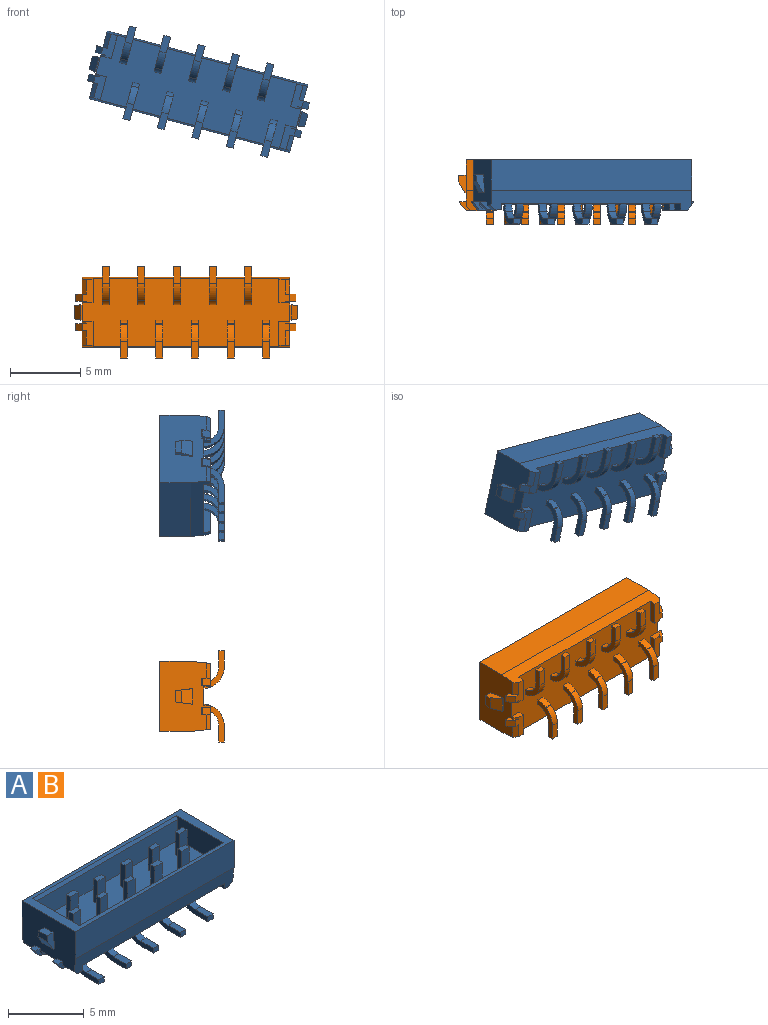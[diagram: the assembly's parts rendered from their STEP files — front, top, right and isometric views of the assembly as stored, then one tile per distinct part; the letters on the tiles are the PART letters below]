
ASSEMBLY  parts=2 mates=1
PART A: 227 faces, bbox 15.9x6.5x4.6 mm
  f0: plane 5x3.3mm, normal (-1,0,0), area 14.7mm2, adj f1,f3,f5,f6,f7,f8,f11,f14
  f1: plane 1.25x0.55mm, normal (0,0.99,0.12), area 0.5mm2, adj f0,f2,f4,f5,f6
  f2: plane 1.11x0.78mm, normal (-0.87,0,-0.5), area 0.9mm2, adj f1,f3,f4,f6
  f3: plane 1.25x0.55mm, normal (0,-0.99,0.12), area 0.5mm2, adj f0,f2,f4,f5,f6
  f4: plane 0.92x0.47mm, normal (-1,0,0), area 0.4mm2, adj f1,f2,f3,f5
  f5: plane 0.8x0.55mm, normal (0,0,1), area 0.4mm2, adj f0,f1,f3,f4
  f6: plane 1.11x0.1mm, normal (0,0,-1), area 0.1mm2, adj f0,f1,f2,f3
  f7: plane 0.5x0.45mm, normal (0,0,1), area 0.2mm2, adj f0,f11,f45,f46
  f8: plane 0.5x0.45mm, normal (0,0,1), area 0.2mm2, adj f0,f14,f112,f113
  f9: plane 0.5x0.45mm, normal (0,0,1), area 0.2mm2, adj f28,f224,f225,f226
  f10: plane 0.5x0.45mm, normal (0,0,1), area 0.2mm2, adj f21,f22,f23,f28
  f11: plane 0.75x0.6mm, normal (0,-1,0), area 0.2mm2, adj f0,f7,f13,f18,f41,f46
  f12: plane 0.54x0.5mm, normal (-0.77,0,-0.64), area 0.4mm2, adj f14,f17,f112,f113
  f13: plane 0.54x0.5mm, normal (-0.77,0,-0.64), area 0.4mm2, adj f11,f18,f45,f46
  f14: plane 0.75x0.6mm, normal (0,1,0), area 0.2mm2, adj f0,f8,f12,f17,f44,f113
  f15: plane 1.68x0.78mm, normal (0,0,-1), area 0.9mm2, adj f19,f21,f23,f24,f25,f35,f48,f51
  f16: plane 1.68x0.78mm, normal (0,0,-1), area 0.9mm2, adj f20,f26,f27,f40,f47,f49,f224,f226
  f17: plane 1.68x0.78mm, normal (0,0,-1), area 0.9mm2, adj f12,f14,f35,f36,f43,f44,f50,f112
  f18: plane 1.68x0.78mm, normal (0,0,-1), area 0.9mm2, adj f11,f13,f37,f39,f41,f42,f45,f47
  f19: plane 0.54x0.5mm, normal (0.77,0,-0.64), area 0.4mm2, adj f15,f21,f22,f23
  f20: plane 0.54x0.5mm, normal (0.77,0,-0.64), area 0.4mm2, adj f16,f224,f225,f226
  f21: plane 0.75x0.6mm, normal (0,1,0), area 0.2mm2, adj f10,f15,f19,f22,f24,f28
  f22: plane 0.5x0.06mm, normal (1,0,0), area 0mm2, adj f10,f19,f21,f23
  f23: plane 0.75x0.6mm, normal (0,-1,0), area 0.2mm2, adj f10,f15,f19,f22,f25,f28
  f24: plane 0.3x0.3mm, normal (0.71,0,-0.71), area 0.1mm2, adj f15,f21,f28,f51
  f25: plane 1.08x0.3mm, normal (0.71,0,-0.71), area 0.5mm2, adj f15,f23,f28,f35
  f26: plane 1.08x0.3mm, normal (0.71,0,-0.71), area 0.5mm2, adj f16,f28,f47,f224
  f27: plane 0.3x0.3mm, normal (0.71,0,-0.71), area 0.1mm2, adj f16,f28,f40,f226
  f28: plane 5x3.3mm, normal (1,0,0), area 14.7mm2, adj f9,f10,f21,f23,f24,f25,f26,f27
  f29: plane 1.25x0.55mm, normal (0,0.99,0.12), area 0.5mm2, adj f28,f30,f31,f33,f34
  f30: plane 1.11x0.78mm, normal (0.87,0,-0.5), area 0.9mm2, adj f29,f31,f32,f34
  f31: plane 1.11x0.1mm, normal (0,0,-1), area 0.1mm2, adj f28,f29,f30,f32
  f32: plane 1.25x0.55mm, normal (0,-0.99,0.12), area 0.5mm2, adj f28,f30,f31,f33,f34
  f33: plane 0.8x0.55mm, normal (0,0,1), area 0.4mm2, adj f28,f29,f32,f34
  f34: plane 0.92x0.47mm, normal (1,0,0), area 0.4mm2, adj f29,f30,f32,f33
  f35: plane 14.78x1.4mm, normal (0,-0.99,-0.1), area 14.7mm2, adj f0,f15,f17,f25,f28,f36,f38,f43
  f36: plane 1.73x0.45mm, normal (1,0,0), area 0.8mm2, adj f17,f35,f38,f50
  f37: plane 1.73x0.45mm, normal (1,0,0), area 0.8mm2, adj f18,f38,f39,f47
  f38: plane 14.78x4.8mm, normal (0,0,-1), area 63.6mm2, adj f0,f28,f35,f36,f37,f39,f40,f47
  f39: plane 0.78x0.45mm, normal (0,-1,0), area 0.3mm2, adj f0,f18,f37,f38,f41
  f40: plane 0.78x0.45mm, normal (0,-1,0), area 0.3mm2, adj f16,f27,f28,f38,f49
  f41: plane 0.3x0.3mm, normal (-0.71,0,-0.71), area 0.1mm2, adj f0,f11,f18,f39
  f42: plane 1.08x0.3mm, normal (-0.71,0,-0.71), area 0.5mm2, adj f0,f18,f45,f47
  f43: plane 1.08x0.3mm, normal (-0.71,0,-0.71), area 0.5mm2, adj f0,f17,f35,f112
  f44: plane 0.3x0.3mm, normal (-0.71,0,-0.71), area 0.1mm2, adj f0,f14,f17,f50
  f45: plane 0.75x0.6mm, normal (0,1,0), area 0.2mm2, adj f0,f7,f13,f18,f42,f46
  f46: plane 0.5x0.06mm, normal (-1,0,0), area 0mm2, adj f7,f11,f13,f45
  f47: plane 14.78x1.4mm, normal (0,0.99,-0.1), area 14.7mm2, adj f0,f16,f18,f26,f28,f37,f38,f42
  f48: plane 1.73x0.45mm, normal (-1,0,0), area 0.8mm2, adj f15,f35,f38,f51
  f49: plane 1.73x0.45mm, normal (-1,0,0), area 0.8mm2, adj f16,f38,f40,f47
  f50: plane 0.78x0.45mm, normal (0,1,0), area 0.3mm2, adj f0,f17,f36,f38,f44
  f51: plane 0.78x0.45mm, normal (0,1,0), area 0.3mm2, adj f15,f24,f28,f38,f48
  f52: plane 14.78x2.2mm, normal (0,1,0), area 32.5mm2, adj f0,f28,f47,f53
  f53: plane 14.78x5mm, normal (0,0,1), area 15mm2, adj f0,f28,f52,f54,f55,f58,f59,f60
  f54: plane 14.78x2.2mm, normal (0,-1,0), area 32.5mm2, adj f0,f28,f35,f53
  f55: plane 4.4x1.85mm, normal (-1,0,0), area 7.6mm2, adj f53,f56,f57,f58,f60,f61
  f56: plane 13.38x4mm, normal (0,0,1), area 50.8mm2, adj f55,f57,f59,f61,f62,f63,f64,f66
  f57: plane 13.38x1.61mm, normal (0,1,0.04), area 21.5mm2, adj f55,f56,f58,f59
  f58: plane 13.38x0.24mm, normal (0,0.87,0.5), area 3.7mm2, adj f53,f55,f57,f59
  f59: plane 4.4x1.85mm, normal (1,0,0), area 7.6mm2, adj f53,f56,f57,f58,f60,f61
  f60: plane 13.38x0.24mm, normal (0,-0.87,0.5), area 3.7mm2, adj f53,f55,f59,f61
  f61: plane 13.38x1.61mm, normal (0,-1,0.04), area 21.5mm2, adj f55,f56,f59,f60
  f62: plane 1.85x0.7mm, normal (0,1,0), area 1.3mm2, adj f56,f63,f65,f66
  f63: plane 1.85x0.39mm, normal (1,0,0), area 0.7mm2, adj f56,f62,f64,f65
  f64: plane 1.85x0.7mm, normal (0,-1,0), area 1.3mm2, adj f56,f63,f65,f66
  f65: plane 0.7x0.39mm, normal (0,0,1), area 0.3mm2, adj f62,f63,f64,f66
  f66: plane 1.85x0.39mm, normal (-1,0,0), area 0.7mm2, adj f56,f62,f64,f65
  f67: plane 1.85x0.7mm, normal (0,-1,0), area 1.3mm2, adj f56,f68,f70,f71
  f68: plane 1.85x0.39mm, normal (-1,0,0), area 0.7mm2, adj f56,f67,f69,f70
  f69: plane 1.85x0.7mm, normal (0,1,0), area 1.3mm2, adj f56,f68,f70,f71
  f70: plane 0.7x0.39mm, normal (0,0,1), area 0.3mm2, adj f67,f68,f69,f71
  f71: plane 1.85x0.39mm, normal (1,0,0), area 0.7mm2, adj f56,f67,f69,f70
  f72: plane 1.85x0.7mm, normal (0,1,0), area 1.3mm2, adj f56,f73,f75,f76
  f73: plane 1.85x0.39mm, normal (1,0,0), area 0.7mm2, adj f56,f72,f74,f75
  f74: plane 1.85x0.7mm, normal (0,-1,0), area 1.3mm2, adj f56,f73,f75,f76
  f75: plane 0.7x0.39mm, normal (0,0,1), area 0.3mm2, adj f72,f73,f74,f76
  f76: plane 1.85x0.39mm, normal (-1,0,0), area 0.7mm2, adj f56,f72,f74,f75
  f77: plane 1.85x0.7mm, normal (0,-1,0), area 1.3mm2, adj f56,f78,f80,f81
  f78: plane 1.85x0.39mm, normal (-1,0,0), area 0.7mm2, adj f56,f77,f79,f80
  f79: plane 1.85x0.7mm, normal (0,1,0), area 1.3mm2, adj f56,f78,f80,f81
  f80: plane 0.7x0.39mm, normal (0,0,1), area 0.3mm2, adj f77,f78,f79,f81
  f81: plane 1.85x0.39mm, normal (1,0,0), area 0.7mm2, adj f56,f77,f79,f80
  f82: plane 1.85x0.7mm, normal (0,1,0), area 1.3mm2, adj f56,f83,f85,f86
  f83: plane 1.85x0.39mm, normal (1,0,0), area 0.7mm2, adj f56,f82,f84,f85
  f84: plane 1.85x0.7mm, normal (0,-1,0), area 1.3mm2, adj f56,f83,f85,f86
  f85: plane 0.7x0.39mm, normal (0,0,1), area 0.3mm2, adj f82,f83,f84,f86
  f86: plane 1.85x0.39mm, normal (-1,0,0), area 0.7mm2, adj f56,f82,f84,f85
  f87: plane 1.85x0.7mm, normal (0,-1,0), area 1.3mm2, adj f56,f88,f90,f91
  f88: plane 1.85x0.39mm, normal (-1,0,0), area 0.7mm2, adj f56,f87,f89,f90
  f89: plane 1.85x0.7mm, normal (0,1,0), area 1.3mm2, adj f56,f88,f90,f91
  f90: plane 0.7x0.39mm, normal (0,0,1), area 0.3mm2, adj f87,f88,f89,f91
  f91: plane 1.85x0.39mm, normal (1,0,0), area 0.7mm2, adj f56,f87,f89,f90
  f92: plane 1.85x0.7mm, normal (0,1,0), area 1.3mm2, adj f56,f93,f95,f96
  f93: plane 1.85x0.39mm, normal (1,0,0), area 0.7mm2, adj f56,f92,f94,f95
  f94: plane 1.85x0.7mm, normal (0,-1,0), area 1.3mm2, adj f56,f93,f95,f96
  f95: plane 0.7x0.39mm, normal (0,0,1), area 0.3mm2, adj f92,f93,f94,f96
  f96: plane 1.85x0.39mm, normal (-1,0,0), area 0.7mm2, adj f56,f92,f94,f95
  f97: plane 1.85x0.7mm, normal (0,-1,0), area 1.3mm2, adj f56,f98,f100,f101
  f98: plane 1.85x0.39mm, normal (-1,0,0), area 0.7mm2, adj f56,f97,f99,f100
  f99: plane 1.85x0.7mm, normal (0,1,0), area 1.3mm2, adj f56,f98,f100,f101
  f100: plane 0.7x0.39mm, normal (0,0,1), area 0.3mm2, adj f97,f98,f99,f101
  f101: plane 1.85x0.39mm, normal (1,0,0), area 0.7mm2, adj f56,f97,f99,f100
  f102: plane 1.85x0.7mm, normal (0,1,0), area 1.3mm2, adj f56,f103,f105,f106
  f103: plane 1.85x0.39mm, normal (1,0,0), area 0.7mm2, adj f56,f102,f104,f105
  f104: plane 1.85x0.7mm, normal (0,-1,0), area 1.3mm2, adj f56,f103,f105,f106
  f105: plane 0.7x0.39mm, normal (0,0,1), area 0.3mm2, adj f102,f103,f104,f106
  f106: plane 1.85x0.39mm, normal (-1,0,0), area 0.7mm2, adj f56,f102,f104,f105
  f107: plane 1.85x0.7mm, normal (0,-1,0), area 1.3mm2, adj f56,f108,f110,f111
  f108: plane 1.85x0.39mm, normal (-1,0,0), area 0.7mm2, adj f56,f107,f109,f110
  f109: plane 1.85x0.7mm, normal (0,1,0), area 1.3mm2, adj f56,f108,f110,f111
  f110: plane 0.7x0.39mm, normal (0,0,1), area 0.3mm2, adj f107,f108,f109,f111
  f111: plane 1.85x0.39mm, normal (1,0,0), area 0.7mm2, adj f56,f107,f109,f110
  f112: plane 0.75x0.6mm, normal (0,-1,0), area 0.2mm2, adj f0,f8,f12,f17,f43,f113
  f113: plane 0.5x0.06mm, normal (-1,0,0), area 0mm2, adj f8,f12,f14,f112
  f114: plane 2.69x1.45mm, normal (-1,0,0), area 1.2mm2, adj f38,f115,f117,f118,f119,f120,f121,f122
  f115: cylinder r=1.5mm len=0.77mm, axis (1,0,0), area 0.4mm2, adj f38,f114,f116,f124
  f116: plane 2.69x1.45mm, normal (1,0,0), area 1.2mm2, adj f38,f115,f117,f118,f119,f120,f121,f122
  f117: cylinder r=1.11mm len=0.55mm, axis (1,0,0), area 0.3mm2, adj f38,f114,f116,f118
  f118: plane 0.5x0.04mm, normal (0,0.82,0.57), area 0mm2, adj f114,f116,f117,f119
  f119: cylinder r=1.11mm len=0.91mm, axis (1,0,0), area 0.5mm2, adj f114,f116,f118,f120
  f120: plane 1.17x0.5mm, normal (0,0,1), area 0.6mm2, adj f114,f116,f119,f121
  f121: plane 0.5x0.39mm, normal (0,1,0), area 0.2mm2, adj f114,f116,f120,f122
  f122: plane 1.17x0.5mm, normal (0,0,-1), area 0.6mm2, adj f114,f116,f121,f123
  f123: cylinder r=1.5mm len=1.23mm, axis (1,0,0), area 0.7mm2, adj f114,f116,f122,f124
  f124: plane 0.5x0.04mm, normal (0,-0.82,-0.57), area 0mm2, adj f114,f115,f116,f123
  f125: plane 2.69x1.45mm, normal (-1,0,0), area 1.2mm2, adj f38,f126,f128,f129,f130,f131,f132,f133
  f126: cylinder r=1.11mm len=0.55mm, axis (1,0,0), area 0.3mm2, adj f38,f125,f127,f135
  f127: plane 2.69x1.45mm, normal (1,0,0), area 1.2mm2, adj f38,f126,f128,f129,f130,f131,f132,f133
  f128: cylinder r=1.5mm len=0.77mm, axis (1,0,0), area 0.4mm2, adj f38,f125,f127,f129
  f129: plane 0.5x0.04mm, normal (0,0.82,-0.57), area 0mm2, adj f125,f127,f128,f130
  f130: cylinder r=1.5mm len=1.23mm, axis (1,0,0), area 0.7mm2, adj f125,f127,f129,f131
  f131: plane 1.17x0.5mm, normal (0,0,-1), area 0.6mm2, adj f125,f127,f130,f132
  f132: plane 0.5x0.39mm, normal (0,-1,0), area 0.2mm2, adj f125,f127,f131,f133
  f133: plane 1.17x0.5mm, normal (0,0,1), area 0.6mm2, adj f125,f127,f132,f134
  f134: cylinder r=1.11mm len=0.91mm, axis (1,0,0), area 0.5mm2, adj f125,f127,f133,f135
  f135: plane 0.5x0.04mm, normal (0,-0.82,0.57), area 0mm2, adj f125,f126,f127,f134
  f136: plane 2.69x1.45mm, normal (-1,0,0), area 1.2mm2, adj f38,f137,f139,f140,f141,f142,f143,f144
  f137: cylinder r=1.5mm len=0.77mm, axis (1,0,0), area 0.4mm2, adj f38,f136,f138,f146
  f138: plane 2.69x1.45mm, normal (1,0,0), area 1.2mm2, adj f38,f137,f139,f140,f141,f142,f143,f144
  f139: cylinder r=1.11mm len=0.55mm, axis (1,0,0), area 0.3mm2, adj f38,f136,f138,f140
  f140: plane 0.5x0.04mm, normal (0,0.82,0.57), area 0mm2, adj f136,f138,f139,f141
  f141: cylinder r=1.11mm len=0.91mm, axis (1,0,0), area 0.5mm2, adj f136,f138,f140,f142
  f142: plane 1.17x0.5mm, normal (0,0,1), area 0.6mm2, adj f136,f138,f141,f143
  f143: plane 0.5x0.39mm, normal (0,1,0), area 0.2mm2, adj f136,f138,f142,f144
  f144: plane 1.17x0.5mm, normal (0,0,-1), area 0.6mm2, adj f136,f138,f143,f145
  f145: cylinder r=1.5mm len=1.23mm, axis (1,0,0), area 0.7mm2, adj f136,f138,f144,f146
  f146: plane 0.5x0.04mm, normal (0,-0.82,-0.57), area 0mm2, adj f136,f137,f138,f145
  f147: plane 2.69x1.45mm, normal (-1,0,0), area 1.2mm2, adj f38,f148,f150,f151,f152,f153,f154,f155
  f148: cylinder r=1.11mm len=0.55mm, axis (1,0,0), area 0.3mm2, adj f38,f147,f149,f157
  f149: plane 2.69x1.45mm, normal (1,0,0), area 1.2mm2, adj f38,f148,f150,f151,f152,f153,f154,f155
  f150: cylinder r=1.5mm len=0.77mm, axis (1,0,0), area 0.4mm2, adj f38,f147,f149,f151
  f151: plane 0.5x0.04mm, normal (0,0.82,-0.57), area 0mm2, adj f147,f149,f150,f152
  f152: cylinder r=1.5mm len=1.23mm, axis (1,0,0), area 0.7mm2, adj f147,f149,f151,f153
  f153: plane 1.17x0.5mm, normal (0,0,-1), area 0.6mm2, adj f147,f149,f152,f154
  f154: plane 0.5x0.39mm, normal (0,-1,0), area 0.2mm2, adj f147,f149,f153,f155
  f155: plane 1.17x0.5mm, normal (0,0,1), area 0.6mm2, adj f147,f149,f154,f156
  f156: cylinder r=1.11mm len=0.91mm, axis (1,0,0), area 0.5mm2, adj f147,f149,f155,f157
  f157: plane 0.5x0.04mm, normal (0,-0.82,0.57), area 0mm2, adj f147,f148,f149,f156
  f158: plane 2.69x1.45mm, normal (-1,0,0), area 1.2mm2, adj f38,f159,f161,f162,f163,f164,f165,f166
  f159: cylinder r=1.5mm len=0.77mm, axis (1,0,0), area 0.4mm2, adj f38,f158,f160,f168
  f160: plane 2.69x1.45mm, normal (1,0,0), area 1.2mm2, adj f38,f159,f161,f162,f163,f164,f165,f166
  f161: cylinder r=1.11mm len=0.55mm, axis (1,0,0), area 0.3mm2, adj f38,f158,f160,f162
  f162: plane 0.5x0.04mm, normal (0,0.82,0.57), area 0mm2, adj f158,f160,f161,f163
  f163: cylinder r=1.11mm len=0.91mm, axis (1,0,0), area 0.5mm2, adj f158,f160,f162,f164
  f164: plane 1.17x0.5mm, normal (0,0,1), area 0.6mm2, adj f158,f160,f163,f165
  f165: plane 0.5x0.39mm, normal (0,1,0), area 0.2mm2, adj f158,f160,f164,f166
  f166: plane 1.17x0.5mm, normal (0,0,-1), area 0.6mm2, adj f158,f160,f165,f167
  f167: cylinder r=1.5mm len=1.23mm, axis (1,0,0), area 0.7mm2, adj f158,f160,f166,f168
  f168: plane 0.5x0.04mm, normal (0,-0.82,-0.57), area 0mm2, adj f158,f159,f160,f167
  f169: plane 2.69x1.45mm, normal (-1,0,0), area 1.2mm2, adj f38,f170,f171,f172,f173,f174,f175,f176
  f170: cylinder r=1.5mm len=0.77mm, axis (1,0,0), area 0.4mm2, adj f38,f169,f171,f179
  f171: plane 0.5x0.04mm, normal (0,0.82,-0.57), area 0mm2, adj f169,f170,f172,f179
  f172: cylinder r=1.5mm len=1.23mm, axis (1,0,0), area 0.7mm2, adj f169,f171,f173,f179
  f173: plane 1.17x0.5mm, normal (0,0,-1), area 0.6mm2, adj f169,f172,f174,f179
  f174: plane 0.5x0.39mm, normal (0,-1,0), area 0.2mm2, adj f169,f173,f175,f179
  f175: plane 1.17x0.5mm, normal (0,0,1), area 0.6mm2, adj f169,f174,f176,f179
  f176: cylinder r=1.11mm len=0.91mm, axis (1,0,0), area 0.5mm2, adj f169,f175,f177,f179
  f177: plane 0.5x0.04mm, normal (0,-0.82,0.57), area 0mm2, adj f169,f176,f178,f179
  f178: cylinder r=1.11mm len=0.55mm, axis (1,0,0), area 0.3mm2, adj f38,f169,f177,f179
  f179: plane 2.69x1.45mm, normal (1,0,0), area 1.2mm2, adj f38,f170,f171,f172,f173,f174,f175,f176
  f180: plane 2.69x1.45mm, normal (-1,0,0), area 1.2mm2, adj f38,f181,f183,f184,f185,f186,f187,f188
  f181: cylinder r=1.5mm len=0.77mm, axis (1,0,0), area 0.4mm2, adj f38,f180,f182,f190
  f182: plane 2.69x1.45mm, normal (1,0,0), area 1.2mm2, adj f38,f181,f183,f184,f185,f186,f187,f188
  f183: cylinder r=1.11mm len=0.55mm, axis (1,0,0), area 0.3mm2, adj f38,f180,f182,f184
  f184: plane 0.5x0.04mm, normal (0,0.82,0.57), area 0mm2, adj f180,f182,f183,f185
  f185: cylinder r=1.11mm len=0.91mm, axis (1,0,0), area 0.5mm2, adj f180,f182,f184,f186
  f186: plane 1.17x0.5mm, normal (0,0,1), area 0.6mm2, adj f180,f182,f185,f187
  f187: plane 0.5x0.39mm, normal (0,1,0), area 0.2mm2, adj f180,f182,f186,f188
  f188: plane 1.17x0.5mm, normal (0,0,-1), area 0.6mm2, adj f180,f182,f187,f189
  f189: cylinder r=1.5mm len=1.23mm, axis (1,0,0), area 0.7mm2, adj f180,f182,f188,f190
  f190: plane 0.5x0.04mm, normal (0,-0.82,-0.57), area 0mm2, adj f180,f181,f182,f189
  f191: plane 2.69x1.45mm, normal (-1,0,0), area 1.2mm2, adj f38,f192,f193,f194,f195,f196,f197,f198
  f192: cylinder r=1.5mm len=0.77mm, axis (1,0,0), area 0.4mm2, adj f38,f191,f193,f201
  f193: plane 0.5x0.04mm, normal (0,0.82,-0.57), area 0mm2, adj f191,f192,f194,f201
  f194: cylinder r=1.5mm len=1.23mm, axis (1,0,0), area 0.7mm2, adj f191,f193,f195,f201
  f195: plane 1.17x0.5mm, normal (0,0,-1), area 0.6mm2, adj f191,f194,f196,f201
  f196: plane 0.5x0.39mm, normal (0,-1,0), area 0.2mm2, adj f191,f195,f197,f201
  f197: plane 1.17x0.5mm, normal (0,0,1), area 0.6mm2, adj f191,f196,f198,f201
  f198: cylinder r=1.11mm len=0.91mm, axis (1,0,0), area 0.5mm2, adj f191,f197,f199,f201
  f199: plane 0.5x0.04mm, normal (0,-0.82,0.57), area 0mm2, adj f191,f198,f200,f201
  f200: cylinder r=1.11mm len=0.55mm, axis (1,0,0), area 0.3mm2, adj f38,f191,f199,f201
  f201: plane 2.69x1.45mm, normal (1,0,0), area 1.2mm2, adj f38,f192,f193,f194,f195,f196,f197,f198
  f202: plane 2.69x1.45mm, normal (-1,0,0), area 1.2mm2, adj f38,f203,f205,f206,f207,f208,f209,f210
  f203: cylinder r=1.5mm len=0.77mm, axis (1,0,0), area 0.4mm2, adj f38,f202,f204,f212
  f204: plane 2.69x1.45mm, normal (1,0,0), area 1.2mm2, adj f38,f203,f205,f206,f207,f208,f209,f210
  f205: cylinder r=1.11mm len=0.55mm, axis (1,0,0), area 0.3mm2, adj f38,f202,f204,f206
  f206: plane 0.5x0.04mm, normal (0,0.82,0.57), area 0mm2, adj f202,f204,f205,f207
  f207: cylinder r=1.11mm len=0.91mm, axis (1,0,0), area 0.5mm2, adj f202,f204,f206,f208
  f208: plane 1.17x0.5mm, normal (0,0,1), area 0.6mm2, adj f202,f204,f207,f209
  f209: plane 0.5x0.39mm, normal (0,1,0), area 0.2mm2, adj f202,f204,f208,f210
  f210: plane 1.17x0.5mm, normal (0,0,-1), area 0.6mm2, adj f202,f204,f209,f211
  f211: cylinder r=1.5mm len=1.23mm, axis (1,0,0), area 0.7mm2, adj f202,f204,f210,f212
  f212: plane 0.5x0.04mm, normal (0,-0.82,-0.57), area 0mm2, adj f202,f203,f204,f211
  f213: plane 2.69x1.45mm, normal (-1,0,0), area 1.2mm2, adj f38,f214,f215,f216,f217,f218,f219,f220
  f214: cylinder r=1.5mm len=0.77mm, axis (1,0,0), area 0.4mm2, adj f38,f213,f215,f223
  f215: plane 0.5x0.04mm, normal (0,0.82,-0.57), area 0mm2, adj f213,f214,f216,f223
  f216: cylinder r=1.5mm len=1.23mm, axis (1,0,0), area 0.7mm2, adj f213,f215,f217,f223
  f217: plane 1.17x0.5mm, normal (0,0,-1), area 0.6mm2, adj f213,f216,f218,f223
  f218: plane 0.5x0.39mm, normal (0,-1,0), area 0.2mm2, adj f213,f217,f219,f223
  f219: plane 1.17x0.5mm, normal (0,0,1), area 0.6mm2, adj f213,f218,f220,f223
  f220: cylinder r=1.11mm len=0.91mm, axis (1,0,0), area 0.5mm2, adj f213,f219,f221,f223
  f221: plane 0.5x0.04mm, normal (0,-0.82,0.57), area 0mm2, adj f213,f220,f222,f223
  f222: cylinder r=1.11mm len=0.55mm, axis (1,0,0), area 0.3mm2, adj f38,f213,f221,f223
  f223: plane 2.69x1.45mm, normal (1,0,0), area 1.2mm2, adj f38,f214,f215,f216,f217,f218,f219,f220
  f224: plane 0.75x0.6mm, normal (0,1,0), area 0.2mm2, adj f9,f16,f20,f26,f28,f225
  f225: plane 0.5x0.06mm, normal (1,0,0), area 0mm2, adj f9,f20,f224,f226
  f226: plane 0.75x0.6mm, normal (0,-1,0), area 0.2mm2, adj f9,f16,f20,f27,f28,f225
PART B: same geometry as A
PLACE A rot(axis=(-0.98,0.13,0.13),91deg) t=(0.89,1.85,15.72)mm
PLACE B rot(axis=(0,0.71,0.71),180deg) t=(0,1.85,0)mm
MATE planar A.f122 <-> B.f210  axis (0,-1,0) through (5.72,-2.75,11.66)mm
